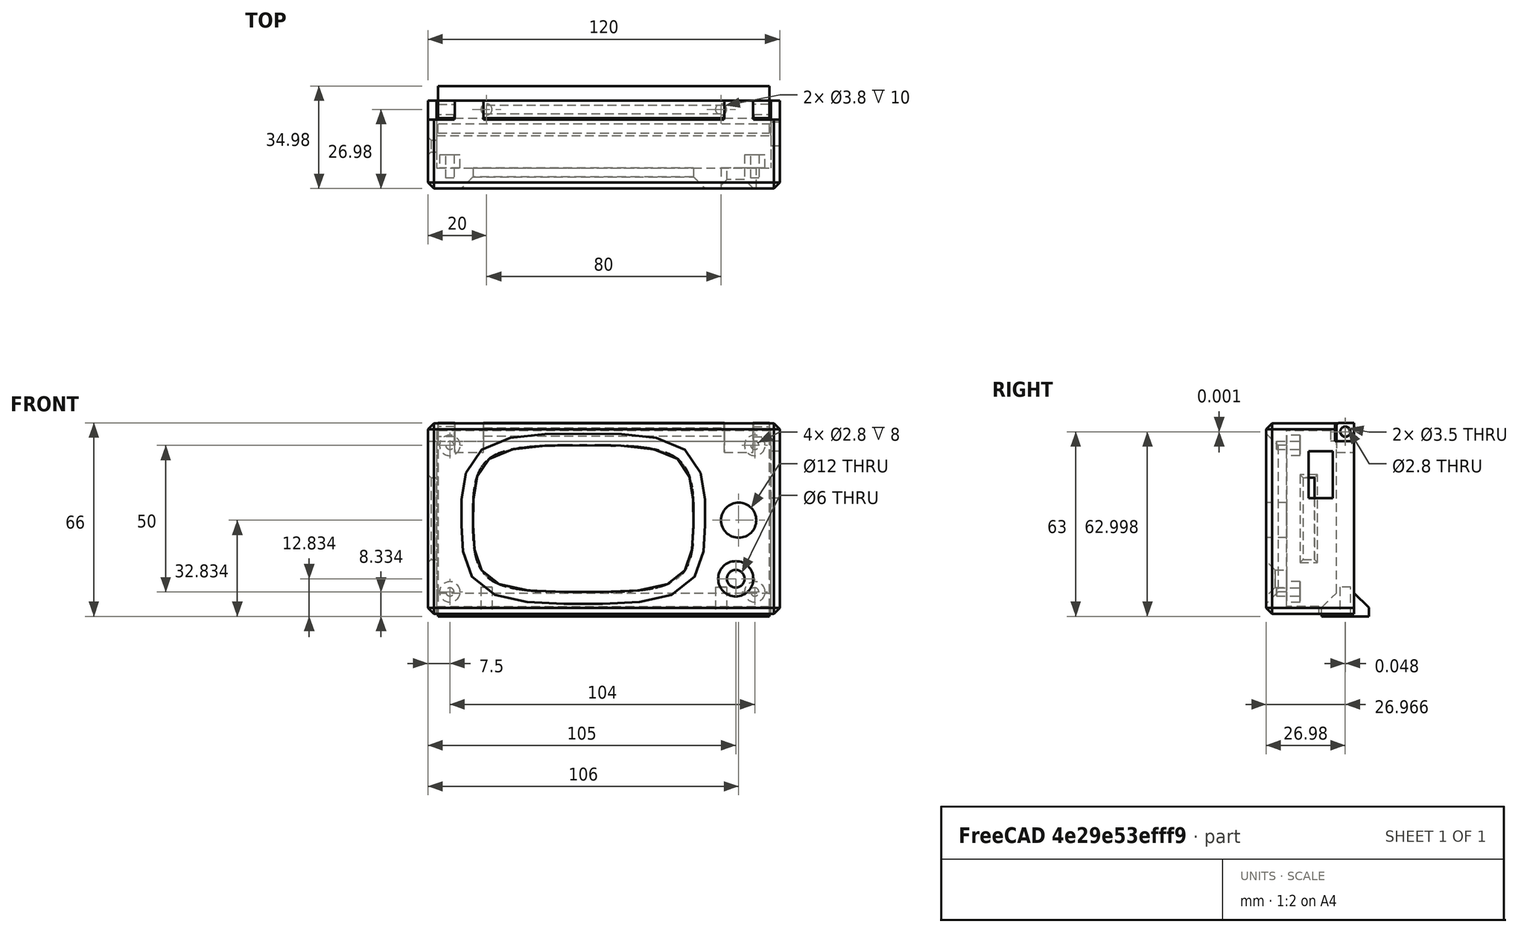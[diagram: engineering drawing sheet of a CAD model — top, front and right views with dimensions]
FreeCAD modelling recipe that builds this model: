
FCSTD DOCUMENT  (FreeCAD 0.19R)
Label: BottomScreen
License: All rights reserved
LicenseURL: http://en.wikipedia.org/wiki/All_rights_reserved
objects: Sketcher::SketchObject×18, PartDesign::Pocket×13, PartDesign::Pad×5, PartDesign::Chamfer×4, PartDesign::Body×2, Mesh::Feature×2, PartDesign::Fillet×1
note: 66 computed .brp shape members not serialized (recipe doc carries the construction recipe); baked Part::Feature solids carry a one-line shape summary decoded from their .brp

FEATURE [Sketcher::SketchObject] Sketch028  label="knob"
  FullyConstrained = false
  MapMode = 5
  Placement = pos=(0,0,0) rot=(1,0,0;3.14159rad)
  sketch-geometry (1):
    g0: Circle CenterX=52 CenterY=20.5 CenterZ=0 NormalX=0 NormalY=0 NormalZ=1 AngleXU=0 Radius=3
  constraints (1):
    c: Diameter(g0) = 6
FEATURE [Sketcher::SketchObject] Sketch029
  FullyConstrained = true
  MapMode = 5
  Support = -> [XY_Plane002]
  sketch-geometry (30):
    g0: LineSegment StartX=-53 StartY=32.5 StartZ=0 EndX=67 EndY=32.5 EndZ=0
    g1: LineSegment StartX=67 StartY=32.5 StartZ=0 EndX=67 EndY=-32.5 EndZ=0
    g2: LineSegment StartX=67 StartY=-32.5 StartZ=0 EndX=-53 EndY=-32.5 EndZ=0
    g3: LineSegment StartX=-53 StartY=-32.5 StartZ=0 EndX=-53 EndY=32.5 EndZ=0
    g4: LineSegment StartX=-37 StartY=24.5 StartZ=0 EndX=37 EndY=24.5 EndZ=0
    g5: LineSegment StartX=37 StartY=24.5 StartZ=0 EndX=37 EndY=-24.5 EndZ=0
    g6: LineSegment StartX=37 StartY=-24.5 StartZ=0 EndX=-37 EndY=-24.5 EndZ=0
    g7: LineSegment StartX=-37 StartY=-24.5 StartZ=0 EndX=-37 EndY=24.5 EndZ=0
    g8: LineSegment StartX=-37.7408 StartY=25.116 StartZ=0 EndX=37.7408 EndY=25.116 EndZ=0
    g9: LineSegment StartX=37.7408 StartY=25.116 StartZ=0 EndX=37.7408 EndY=-25.116 EndZ=0
    g10: LineSegment StartX=37.7408 StartY=-25.116 StartZ=0 EndX=-37.7408 EndY=-25.116 EndZ=0
    g11: LineSegment StartX=-37.7408 StartY=-25.116 StartZ=0 EndX=-37.7408 EndY=25.116 EndZ=0
    g12-g19: Circle x8 (B-spline internal-alignment scaffolding for g20; pole/knot coordinates omitted)
    g20: BSplineCurve PolesCount=8 KnotsCount=9 Degree=3 IsPeriodic=1
    g21-g29: GeomPoint x9 (B-spline internal-alignment scaffolding for g20; pole/knot coordinates omitted)
  constraints (53):
    c: Coincident(g0,g1)
    c: Coincident(g1,g2)
    c: Coincident(g2,g3)
    c: Coincident(g3,g0)
    c: Horizontal(g0)
    c: Horizontal(g2)
    c: Vertical(g1)
    c: Vertical(g3)
    c: Coincident(g4,g5)
    c: Coincident(g5,g6)
    c: Coincident(g6,g7)
    c: Coincident(g7,g4)
    c: Horizontal(g4)
    c: Vertical(g7)
    c: Distance(g5) = 49
    c: Distance(g4,g3) = 16
    c: Distance(g0,g5) = 30
    c: Distance(g6,g2) = 8
    c: Distance(g4,g0) = 8
    c: Distance(g6) = 74
    c: Symmetric(g5,g6,g-2)
    c: Symmetric(g5,g4,g-1)
    c: Coincident(g8,g9)
    c: Coincident(g9,g10)
    c: Coincident(g10,g11)
    c: Coincident(g11,g8)
    c: Horizontal(g8)
    c: Horizontal(g10)
    c: Vertical(g9)
    c: Vertical(g11)
    c: Symmetric(g9,g8,g-1)
    c: Weight(g12) = 1
    c: Equal(g12,g13)
    c: Equal(g12,g14)
    c: Equal(g12,g15)
    c: PointOnObject(g15,g-1)
    c: Equal(g12,g16)
    c: Equal(g12,g17)
    c: PointOnObject(g17,g-2)
    c: Equal(g12,g18)
    c: Equal(g12,g19)
    c: InternalAlignment(g12-g19 -> g20) x8
    c: InternalAlignment(g21-g29 -> g20) x9
    c: Coincident(g8,g12)
    c: Coincident(g14,g8)
    c: Coincident(g16,g10)
    c: Coincident(g18,g9)
    c: Distance(g19,g5) = 0.5
    c: Symmetric(g19,g15,g-2)
    c: Distance(g17,g6) = 0.5
    c: Symmetric(g17,g13,g-1)
    c: DistanceX(g8) = 37.7408
    c: DistanceY(g8) = 25.116
FEATURE [PartDesign::Pad] Pad005
  Direction = (1,1,1)
  Length = 30
  Length2 = 100
  Profile = -> Sketch029
  Type = 0
FEATURE [PartDesign::Pocket] Pocket016
  BaseFeature = -> Pad005
  Length = 5
  Length2 = 100
  Profile = -> Sketch028
  Type = 1
FEATURE [Sketcher::SketchObject] Sketch001  label="knob001"
  FullyConstrained = false
  MapMode = 5
  Placement = pos=(0,0,30) rot=(0,0,1;0rad)
  Support = -> [Pocket016]
  sketch-geometry (1):
    g0: Circle CenterX=53 CenterY=-0.5 CenterZ=0 NormalX=0 NormalY=0 NormalZ=1 AngleXU=0 Radius=6
  constraints (2):
    c: Diameter(g0) = 12
    c: DistanceY(g0) = -0.5
FEATURE [PartDesign::Pocket] Pocket017
  BaseFeature = -> Pocket016
  Length = 5
  Length2 = 100
  Profile = -> Sketch001
  Type = 1
FEATURE [Sketcher::SketchObject] Sketch030  label="BodyPocket"
  ExternalGeometry = -> [Pocket017]
  FullyConstrained = true
  MapMode = 5
  Placement = pos=(0,0,0) rot=(1,0,0;3.14159rad)
  Support = -> [Pocket017]
  sketch-geometry (4):
    g0: LineSegment StartX=-50 StartY=30 StartZ=0 EndX=64 EndY=30 EndZ=0
    g1: LineSegment StartX=64 StartY=30 StartZ=0 EndX=64 EndY=-30 EndZ=0
    g2: LineSegment StartX=64 StartY=-30 StartZ=0 EndX=-50 EndY=-30 EndZ=0
    g3: LineSegment StartX=-50 StartY=-30 StartZ=0 EndX=-50 EndY=30 EndZ=0
  constraints (12):
    c: Coincident(g0,g1)
    c: Coincident(g1,g2)
    c: Coincident(g2,g3)
    c: Coincident(g3,g0)
    c: Horizontal(g0)
    c: Horizontal(g2)
    c: Vertical(g1)
    c: DistanceX(g0) = -50
    c: DistanceY(g0) = 30
    c: DistanceX(g1) = 64
    c: DistanceY(g2) = -30
    c: Vertical(g3)
FEATURE [PartDesign::Pocket] Pocket018
  BaseFeature = -> Pocket017
  Length = 23
  Length2 = 100
  Profile = -> Sketch030
  Type = 0
FEATURE [PartDesign::Chamfer] Chamfer001
  Angle = 45
  Base = -> Pocket018 [Edge19]
  BaseFeature = -> Pocket018
  ChamferType = 0
  FlipDirection = false
  Size = 4
  Size2 = 1
  SupportTransform = false
FEATURE [Sketcher::SketchObject] Sketch031  label="standofs"
  FullyConstrained = true
  MapMode = 5
  Placement = pos=(0,0,23) rot=(1,0,0;3.14159rad)
  Support = -> [Chamfer001]
  sketch-geometry (4):
    g0: Circle CenterX=-45.5 CenterY=25 CenterZ=0 NormalX=0 NormalY=0 NormalZ=1 AngleXU=0 Radius=3.5
    g1: Circle CenterX=-45.5 CenterY=-25 CenterZ=0 NormalX=0 NormalY=0 NormalZ=1 AngleXU=0 Radius=3.5
    g2: Circle CenterX=58.5 CenterY=-25 CenterZ=0 NormalX=0 NormalY=0 NormalZ=1 AngleXU=0 Radius=3.5
    g3: Circle CenterX=58.5 CenterY=25 CenterZ=0 NormalX=0 NormalY=0 NormalZ=1 AngleXU=0 Radius=3.5
  constraints (10):
    c: Diameter(g0) = 7
    c: Equal(g0,g1)
    c: Equal(g0,g3)
    c: Equal(g0,g2)
    c: Symmetric(g1,g0,g-1)
    c: Symmetric(g2,g3,g-1)
    c: Distance(g3,g2) = 50
    c: Distance(g1,g0) = 50
    c: Distance(g3,g0) = 104
    c: DistanceX(g0) = -45.5
FEATURE [PartDesign::Pad] Pad006
  BaseFeature = -> Chamfer001
  Direction = (1,1,1)
  Length = 4.5
  Length2 = 100
  Profile = -> Sketch031
  Type = 0
FEATURE [Sketcher::SketchObject] Sketch032  label="holes"
  FullyConstrained = true
  MapMode = 5
  Placement = pos=(0,0,18.5) rot=(1,0,0;3.14159rad)
  Support = -> [Pad006]
  sketch-geometry (4):
    g0: Circle CenterX=-45.5 CenterY=25 CenterZ=0 NormalX=0 NormalY=0 NormalZ=1 AngleXU=0 Radius=1.4
    g1: Circle CenterX=58.5 CenterY=25 CenterZ=0 NormalX=0 NormalY=0 NormalZ=1 AngleXU=0 Radius=1.4
    g2: Circle CenterX=58.5 CenterY=-25 CenterZ=0 NormalX=0 NormalY=0 NormalZ=1 AngleXU=0 Radius=1.4
    g3: Circle CenterX=-45.5 CenterY=-25 CenterZ=0 NormalX=0 NormalY=0 NormalZ=1 AngleXU=0 Radius=1.4
  constraints (10):
    c: Distance(g3,g2) = 104
    c: Distance(g3,g0) = 50
    c: Symmetric(g3,g0,g-1)
    c: Symmetric(g2,g1,g-1)
    c: Diameter(g1) = 2.8
    c: Equal(g1,g2)
    c: Equal(g1,g3)
    c: Equal(g1,g0)
    c: DistanceX(g0) = -45.5
    c: Distance(g1,g2) = 50
FEATURE [PartDesign::Pocket] Pocket019
  BaseFeature = -> Pad006
  Length = 8
  Length2 = 100
  Profile = -> Sketch032
  Type = 0
FEATURE [Sketcher::SketchObject] Sketch033
  ExternalGeometry = -> [Pocket019]
  FullyConstrained = true
  MapMode = 5
  Placement = pos=(67,0,0) rot=(0.57735,0.57735,0.57735;2.0944rad)
  Support = -> [Pocket019]
  sketch-geometry (4):
    g0: LineSegment StartX=7 StartY=15.5 StartZ=0 EndX=23 EndY=15.5 EndZ=0
    g1: LineSegment StartX=23 StartY=15.5 StartZ=0 EndX=23 EndY=0 EndZ=0
    g2: LineSegment StartX=23 StartY=0 StartZ=0 EndX=7 EndY=0 EndZ=0
    g3: LineSegment StartX=7 StartY=0 StartZ=0 EndX=7 EndY=15.5 EndZ=0
  constraints (12):
    c: Coincident(g0,g1)
    c: Coincident(g1,g2)
    c: Coincident(g2,g3)
    c: Coincident(g3,g0)
    c: Horizontal(g0)
    c: Horizontal(g2)
    c: Vertical(g1)
    c: Vertical(g3)
    c: Distance(g-3,g0) = 3
    c: Distance(g0) = 16
    c: Distance(g0,g-4) = 7
    c: PointOnObject(g1,g-1)
FEATURE [PartDesign::Pocket] Pocket020
  BaseFeature = -> Pocket019
  Length = 9
  Length2 = 100
  Profile = -> Sketch033
  Type = 0
FEATURE [Sketcher::SketchObject] Sketch034  label="SD"
  ExternalGeometry = -> [Pocket020]
  FullyConstrained = true
  MapMode = 5
  Placement = pos=(-53,0,0) rot=(0.57735,-0.57735,-0.57735;2.0944rad)
  Support = -> [Pocket020]
  sketch-geometry (4):
    g0: LineSegment StartX=-14 StartY=17.5 StartZ=0 EndX=14 EndY=17.5 EndZ=0
    g1: LineSegment StartX=14 StartY=17.5 StartZ=0 EndX=14 EndY=13.5 EndZ=0
    g2: LineSegment StartX=14 StartY=13.5 StartZ=0 EndX=-14 EndY=13.5 EndZ=0
    g3: LineSegment StartX=-14 StartY=13.5 StartZ=0 EndX=-14 EndY=17.5 EndZ=0
  constraints (11):
    c: Coincident(g0,g1)
    c: Coincident(g1,g2)
    c: Coincident(g2,g3)
    c: Coincident(g3,g0)
    c: Horizontal(g0)
    c: Vertical(g1)
    c: Vertical(g3)
    c: Distance(g0,g-3) = 1
    c: Distance(g1) = 4
    c: Symmetric(g1,g2,g-2)
    c: Distance(g2) = 28
FEATURE [PartDesign::Pocket] Pocket021
  BaseFeature = -> Pocket020
  Length = 5
  Length2 = 100
  Profile = -> Sketch034
  Type = 0
FEATURE [Sketcher::SketchObject] Sketch041
  FullyConstrained = true
  MapMode = 5
  Placement = pos=(0,0,0) rot=(0.57735,0.57735,0.57735;2.0944rad)
  Support = -> [YZ_Plane]
  sketch-geometry (9):
    g0: LineSegment StartX=-11 StartY=0 StartZ=0 EndX=-11 EndY=3 EndZ=0
    g1: LineSegment StartX=-11 StartY=3 StartZ=0 EndX=-6 EndY=8 EndZ=0
    g2: LineSegment StartX=-6 StartY=8 StartZ=0 EndX=-6 EndY=66 EndZ=0
    g3: LineSegment StartX=-6 StartY=66 StartZ=0 EndX=0 EndY=66 EndZ=0
    g4: LineSegment StartX=-11 StartY=0 StartZ=0 EndX=0 EndY=0 EndZ=0
    g5: LineSegment StartX=0 StartY=66 StartZ=0 EndX=0 EndY=8 EndZ=0
    g6: LineSegment StartX=0 StartY=8 StartZ=0 EndX=5 EndY=3 EndZ=0
    g7: LineSegment StartX=5 StartY=3 StartZ=0 EndX=5 EndY=0 EndZ=0
    g8: LineSegment StartX=0 StartY=0 StartZ=0 EndX=5 EndY=0 EndZ=0
  constraints (26):
    c: PointOnObject(g3,g-2)
    c: DistanceY(g3) = 66
    c: PointOnObject(g0,g-1)
    c: Vertical(g0)
    c: Coincident(g0,g1)
    c: Coincident(g1,g2)
    c: Vertical(g2)
    c: Coincident(g2,g3)
    c: Coincident(g4,g0)
    c: Coincident(g4,g-1)
    c: Horizontal(g3)
    c: DistanceX(g2) = -6
    c: Distance(g4) = 11
    c: Distance(g0) = 3
    c: Angle(g1) = 0.785398
    c: Coincident(g5,g3)
    c: PointOnObject(g5,g-2)
    c: Coincident(g6,g5)
    c: Coincident(g7,g6)
    c: PointOnObject(g7,g-1)
    c: Coincident(g8,g4)
    c: Coincident(g8,g7)
    c: Vertical(g7)
    c: Distance(g7) = 3
    c: Distance(g8) = 5
    c: Angle(g6) = -0.785398
FEATURE [PartDesign::Pad] Pad
  Direction = (1,1,1)
  Length = 113
  Length2 = 100
  Midplane = true
  Placement = pos=(0,0,0) rot=(0.57735,0.57735,0.57735;2.0944rad)
  Profile = -> Sketch041
  Type = 0
FEATURE [Sketcher::SketchObject] Sketch047
  ExternalGeometry = -> [Pocket021]
  FullyConstrained = false
  MapMode = 5
  Placement = pos=(0,-32.5,0) rot=(1,0,0;1.5708rad)
  Support = -> [Pocket021]
  sketch-geometry (4):
    g0: LineSegment StartX=-50 StartY=12 StartZ=0 EndX=64 EndY=12 EndZ=0
    g1: LineSegment StartX=64 StartY=12 StartZ=0 EndX=64 EndY=-7.27201 EndZ=0
    g2: LineSegment StartX=64 StartY=-7.27201 StartZ=0 EndX=-50 EndY=-7.27201 EndZ=0
    g3: LineSegment StartX=-50 StartY=-7.27201 StartZ=0 EndX=-50 EndY=12 EndZ=0
  constraints (11):
    c: Coincident(g0,g1)
    c: Coincident(g1,g2)
    c: Coincident(g2,g3)
    c: Coincident(g3,g0)
    c: Horizontal(g2)
    c: Vertical(g1)
    c: Vertical(g3)
    c: DistanceY(g0) = 12
    c: DistanceX(g0) = -50
    c: DistanceX(g0) = 64
    c: Horizontal(g0)
FEATURE [PartDesign::Pocket] Pocket
  BaseFeature = -> Pocket021
  Length = 5
  Length2 = 100
  Profile = -> Sketch047
  Type = 0
FEATURE [Sketcher::SketchObject] Sketch
  ExternalGeometry = -> [Pocket]
  FullyConstrained = false
  MapMode = 5
  Placement = pos=(0,32.5,0) rot=(0,0.707107,0.707107;3.14159rad)
  Support = -> [Pocket]
  sketch-geometry (20):
    g0: LineSegment StartX=-69.7312 StartY=6.5 StartZ=0 EndX=-58 EndY=6.5 EndZ=0
    g1: LineSegment StartX=-58 StartY=6.5 StartZ=0 EndX=-58 EndY=-6.37632 EndZ=0
    g2: LineSegment StartX=-58 StartY=-6.37632 StartZ=0 EndX=-69.7312 EndY=-6.37632 EndZ=0
    g3: LineSegment StartX=-69.7312 StartY=-6.37632 StartZ=0 EndX=-69.7312 EndY=6.5 EndZ=0
    g4: LineSegment StartX=-48 StartY=-9.0631 StartZ=0 EndX=-48 EndY=6.5 EndZ=0
    g5: LineSegment StartX=-32 StartY=6.5 StartZ=0 EndX=-26 EndY=6.5 EndZ=0
    g6: LineSegment StartX=-26 StartY=6.5 StartZ=0 EndX=-26 EndY=-4.42544 EndZ=0
    g7: LineSegment StartX=-26 StartY=-4.42544 StartZ=0 EndX=-32 EndY=-4.42544 EndZ=0
    g8: LineSegment StartX=-32 StartY=-4.42544 StartZ=0 EndX=-32 EndY=6.5 EndZ=0
    g9: LineSegment StartX=-16 StartY=6.5 StartZ=0 EndX=-10 EndY=6.5 EndZ=0
    g10: LineSegment StartX=-10 StartY=6.5 StartZ=0 EndX=-10 EndY=-4.36785 EndZ=0
    g11: LineSegment StartX=-10 StartY=-4.36785 StartZ=0 EndX=-16 EndY=-4.36785 EndZ=0
    g12: LineSegment StartX=-16 StartY=-4.36785 StartZ=0 EndX=-16 EndY=6.5 EndZ=0
    g13: LineSegment StartX=56.4953 StartY=6.5 StartZ=0 EndX=44 EndY=6.5 EndZ=0
    g14: LineSegment StartX=44 StartY=6.5 StartZ=0 EndX=44 EndY=-6.05703 EndZ=0
    g15: LineSegment StartX=44 StartY=-6.05703 StartZ=0 EndX=56.4953 EndY=-6.05703 EndZ=0
    g16: LineSegment StartX=56.4953 StartY=-6.05703 StartZ=0 EndX=56.4953 EndY=6.5 EndZ=0
    g17: LineSegment StartX=34 StartY=6.5 StartZ=0 EndX=-48 EndY=6.5 EndZ=0
    g18: LineSegment StartX=-48 StartY=-9.0631 StartZ=0 EndX=34 EndY=-9.0631 EndZ=0
    g19: LineSegment StartX=34 StartY=-9.0631 StartZ=0 EndX=34 EndY=6.5 EndZ=0
  constraints (52):
    c: Coincident(g0,g1)
    c: Coincident(g1,g2)
    c: Coincident(g2,g3)
    c: Coincident(g3,g0)
    c: Horizontal(g0)
    c: Horizontal(g2)
    c: Vertical(g1)
    c: Vertical(g3)
    c: Distance(g0,g-3) = 9
    c: DistanceY(g0) = 6.5
    c: Vertical(g4)
    c: DistanceX(g0,g4) = 10
    c: Coincident(g5,g6)
    c: Coincident(g6,g7)
    c: Coincident(g7,g8)
    c: Coincident(g8,g5)
    c: Horizontal(g5)
    c: Horizontal(g7)
    c: Vertical(g6)
    c: Vertical(g8)
    c: Coincident(g9,g10)
    c: Coincident(g10,g11)
    c: Coincident(g11,g12)
    c: Coincident(g12,g9)
    c: Horizontal(g9)
    c: Horizontal(g11)
    c: Vertical(g10)
    c: Vertical(g12)
    c: Distance(g5) = 6
    c: DistanceX(g5,g9) = 10
    c: Distance(g9) = 6
    c: DistanceY(g9) = 6.5
    c: DistanceY(g5) = 6.5
    c: Coincident(g13,g14)
    c: Coincident(g14,g15)
    c: Coincident(g15,g16)
    c: Coincident(g16,g13)
    c: Horizontal(g13)
    c: Horizontal(g15)
    c: Vertical(g14)
    c: Vertical(g16)
    c: Coincident(g18,g19)
    c: Coincident(g19,g17)
    c: Horizontal(g17)
    c: Horizontal(g18)
    c: Vertical(g19)
    c: DistanceY(g17) = 6.5
    c: DistanceY(g13) = 6.5
    c: Distance(g13,g-4) = 9
    c: DistanceX(g17,g13) = 10
    c: Coincident(g18,g4)
    c: Coincident(g17,g4)
FEATURE [Sketcher::SketchObject] Sketch048
  ExternalGeometry = -> [Pocket]
  FullyConstrained = true
  MapMode = 5
  Placement = pos=(0,0,0) rot=(1,0,0;3.14159rad)
  Support = -> [Pocket]
  sketch-geometry (4):
    g0: LineSegment StartX=-53 StartY=-26.5 StartZ=0 EndX=67 EndY=-26.5 EndZ=0
    g1: LineSegment StartX=67 StartY=-26.5 StartZ=0 EndX=67 EndY=-32 EndZ=0
    g2: LineSegment StartX=67 StartY=-32 StartZ=0 EndX=-53 EndY=-32 EndZ=0
    g3: LineSegment StartX=-53 StartY=-32 StartZ=0 EndX=-53 EndY=-26.5 EndZ=0
  constraints (12):
    c: Coincident(g0,g1)
    c: Coincident(g1,g2)
    c: Coincident(g2,g3)
    c: Coincident(g3,g0)
    c: Horizontal(g0)
    c: Horizontal(g2)
    c: Vertical(g1)
    c: Vertical(g3)
    c: DistanceY(g1) = -32
    c: DistanceX(g0) = 67
    c: DistanceX(g0) = -53
    c: Distance(g0,g-3) = 6
FEATURE [PartDesign::Pad] Pad007
  BaseFeature = -> Pocket
  Direction = (1,1,1)
  Length = 8
  Length2 = 100
  Profile = -> Sketch048
  Reversed = true
  Type = 0
FEATURE [PartDesign::Pocket] Pocket032
  BaseFeature = -> Pad007
  Length = 6
  Length2 = 100
  Profile = -> Sketch
  Type = 0
FEATURE [Sketcher::SketchObject] Sketch049
  FullyConstrained = false
  MapMode = 5
  Placement = pos=(-2.56e-14,3.66e-14,66) rot=(0,0,-1;1.5708rad)
  Support = -> [Pad]
  sketch-geometry (16):
    g0: LineSegment StartX=-3.15788 StartY=61.4961 StartZ=0 EndX=6.80578 EndY=61.4961 EndZ=0
    g1: LineSegment StartX=6.80578 StartY=61.4961 StartZ=0 EndX=6.80578 EndY=56.6425 EndZ=0
    g2: LineSegment StartX=6.80578 StartY=56.6425 StartZ=0 EndX=-3.15788 EndY=56.6425 EndZ=0
    g3: LineSegment StartX=-3.15788 StartY=56.6425 StartZ=0 EndX=-3.15788 EndY=61.4961 EndZ=0
    g4: LineSegment StartX=-4.59158 StartY=50.904 StartZ=0 EndX=9.82769 EndY=50.904 EndZ=0
    g5: LineSegment StartX=9.82769 StartY=50.904 StartZ=0 EndX=9.82769 EndY=41.104 EndZ=0
    g6: LineSegment StartX=9.82769 StartY=41.104 StartZ=0 EndX=-4.59158 EndY=41.104 EndZ=0
    g7: LineSegment StartX=-4.59158 StartY=41.104 StartZ=0 EndX=-4.59158 EndY=50.904 EndZ=0
    g8: LineSegment StartX=-6.16671 StartY=-41.0394 StartZ=0 EndX=7.99909 EndY=-41.0394 EndZ=0
    g9: LineSegment StartX=7.99909 StartY=-41.0394 StartZ=0 EndX=7.99909 EndY=-50.8394 EndZ=0
    g10: LineSegment StartX=7.99909 StartY=-50.8394 StartZ=0 EndX=-6.16671 EndY=-50.8394 EndZ=0
    g11: LineSegment StartX=-6.16671 StartY=-50.8394 StartZ=0 EndX=-6.16671 EndY=-41.0394 EndZ=0
    g12: LineSegment StartX=-2.49543 StartY=-56.9158 StartZ=0 EndX=6.75431 EndY=-56.9158 EndZ=0
    g13: LineSegment StartX=6.75431 StartY=-56.9158 StartZ=0 EndX=6.75431 EndY=-60.1158 EndZ=0
    g14: LineSegment StartX=6.75431 StartY=-60.1158 StartZ=0 EndX=-2.49543 EndY=-60.1158 EndZ=0
    g15: LineSegment StartX=-2.49543 StartY=-60.1158 StartZ=0 EndX=-2.49543 EndY=-56.9158 EndZ=0
  constraints (35):
    c: Coincident(g0,g1)
    c: Coincident(g1,g2)
    c: Coincident(g2,g3)
    c: Coincident(g3,g0)
    c: Horizontal(g0)
    c: Horizontal(g2)
    c: Vertical(g1)
    c: Vertical(g3)
    c: Coincident(g4,g5)
    c: Coincident(g5,g6)
    c: Coincident(g6,g7)
    c: Coincident(g7,g4)
    c: Horizontal(g4)
    c: Horizontal(g6)
    c: Vertical(g5)
    c: Vertical(g7)
    c: Coincident(g8,g9)
    c: Coincident(g9,g10)
    c: Coincident(g10,g11)
    c: Coincident(g11,g8)
    c: Horizontal(g8)
    c: Horizontal(g10)
    c: Vertical(g9)
    c: Vertical(g11)
    c: Coincident(g12,g13)
    c: Coincident(g13,g14)
    c: Coincident(g14,g15)
    c: Coincident(g15,g12)
    c: Horizontal(g12)
    c: Horizontal(g14)
    c: Vertical(g13)
    c: Vertical(g15)
    c: Distance(g13) = 3.2
    c: Distance(g9) = 9.8
    c: Distance(g5) = 9.8
FEATURE [PartDesign::Pocket] Pocket033
  BaseFeature = -> Pad
  Length = 10
  Length2 = 100
  Placement = pos=(0,0,0) rot=(0.57735,0.57735,0.57735;2.0944rad)
  Profile = -> Sketch049
  Type = 0
FEATURE [Sketcher::SketchObject] Sketch050
  ExternalGeometry = -> [Pocket033]
  FullyConstrained = true
  MapMode = 5
  Placement = pos=(56.5,-3.76e-14,2.51e-14) rot=(0.57735,0.57735,0.57735;2.0944rad)
  Support = -> [Pocket033]
  sketch-geometry (1):
    g0: Circle CenterX=-3 CenterY=63 CenterZ=0 NormalX=0 NormalY=0 NormalZ=1 AngleXU=0 Radius=1.4
  constraints (3):
    c: DistanceX(g0) = -3
    c: DistanceY(g0) = 63
    c: Diameter(g0) = 2.8
FEATURE [PartDesign::Pocket] Pocket034
  BaseFeature = -> Pocket033
  Length = 5
  Length2 = 100
  Placement = pos=(0,0,0) rot=(0.57735,0.57735,0.57735;2.0944rad)
  Profile = -> Sketch050
  Type = 1
FEATURE [Sketcher::SketchObject] Sketch051
  FullyConstrained = false
  MapMode = 5
  Placement = pos=(56.5,-5.02e-14,3.14e-14) rot=(0.57735,0.57735,0.57735;2.0944rad)
  Support = -> [Pocket034]
  sketch-geometry (1):
    g0: Circle CenterX=-2.96574 CenterY=62.9984 CenterZ=0 NormalX=0 NormalY=0 NormalZ=1 AngleXU=0 Radius=1.75
  constraints (1):
    c: Diameter(g0) = 3.5
FEATURE [PartDesign::Pocket] Pocket035
  BaseFeature = -> Pocket034
  Length = 7
  Length2 = 100
  Placement = pos=(0,0,0) rot=(0.57735,0.57735,0.57735;2.0944rad)
  Profile = -> Sketch051
  Type = 0
FEATURE [Sketcher::SketchObject] Sketch052
  FullyConstrained = false
  MapMode = 5
  Placement = pos=(-56.5,6.27e-14,-3.76e-14) rot=(-0.57735,-0.57735,0.57735;2.0944rad)
  Support = -> [Pocket035]
  sketch-geometry (1):
    g0: Circle CenterX=-3.01386 CenterY=-62.9994 CenterZ=0 NormalX=0 NormalY=0 NormalZ=1 AngleXU=0 Radius=1.75
  constraints (1):
    c: Diameter(g0) = 3.5
FEATURE [PartDesign::Pocket] Pocket036
  BaseFeature = -> Pocket035
  Length = 7
  Length2 = 100
  Placement = pos=(0,0,0) rot=(0.57735,0.57735,0.57735;2.0944rad)
  Profile = -> Sketch052
  Type = 0
FEATURE [Sketcher::SketchObject] Sketch053
  FullyConstrained = true
  MapMode = 5
  Placement = pos=(0,0,6e-14) rot=(0.707107,0.707107,0;3.14159rad)
  Support = -> [Pocket036]
  sketch-geometry (2):
    g0: Circle CenterX=-3 CenterY=40 CenterZ=0 NormalX=0 NormalY=0 NormalZ=1 AngleXU=0 Radius=1.9
    g1: Circle CenterX=-3 CenterY=-40 CenterZ=0 NormalX=0 NormalY=0 NormalZ=1 AngleXU=0 Radius=1.9
  constraints (5):
    c: Symmetric(g1,g0,g-1)
    c: Diameter(g1) = 3.8
    c: Equal(g1,g0)
    c: Distance(g1,g0) = 80
    c: DistanceX(g0) = -3
FEATURE [PartDesign::Pocket] Pocket037
  BaseFeature = -> Pocket036
  Length = 10
  Length2 = 100
  Placement = pos=(0,0,0) rot=(0.57735,0.57735,0.57735;2.0944rad)
  Profile = -> Sketch053
  Type = 0
FEATURE [PartDesign::Fillet] Fillet
  Base = -> Pocket037 [Edge36,Edge40,Edge32]
  BaseFeature = -> Pocket037
  Placement = pos=(0,0,0) rot=(0.57735,0.57735,0.57735;2.0944rad)
  Radius = 1
  SupportTransform = false
FEATURE [PartDesign::Body] Body  label="Hinge"
  Group = -> [Sketch041,Pad,Sketch049,Pocket033,Sketch050,Pocket034,Sketch051,Pocket035,Sketch052,Pocket036,Sketch053,Pocket037,Fillet]
  Origin = -> Origin
  Placement = pos=(-1.5,0,0) rot=(0,0,1;0rad)
  Tip = -> Fillet
FEATURE [PartDesign::Chamfer] Chamfer
  Angle = 45
  Base = -> Pocket032 [Edge19,Edge4,Edge2,Edge42,Edge5,Edge3,Edge27,Edge20]
  BaseFeature = -> Pocket032
  ChamferType = 0
  FlipDirection = false
  Size = 2
  Size2 = 1
  SupportTransform = false
FEATURE [PartDesign::Chamfer] Chamfer002
  Angle = 45
  Base = -> Chamfer [Edge68,Edge66,Edge67,Edge69]
  BaseFeature = -> Chamfer
  ChamferType = 0
  FlipDirection = false
  Size = 1
  Size2 = 1
  SupportTransform = false
FEATURE [PartDesign::Chamfer] Chamfer003
  Angle = 45
  Base = -> Chamfer002 [Edge70]
  BaseFeature = -> Chamfer002
  ChamferType = 0
  FlipDirection = false
  Size = 3
  Size2 = 1
  SupportTransform = false
FEATURE [Sketcher::SketchObject] Sketch054
  FullyConstrained = false
  MapMode = 5
  Placement = pos=(67,0,0) rot=(0.57735,0.57735,0.57735;2.0944rad)
  Support = -> [Chamfer003]
  sketch-geometry (4):
    g0: LineSegment StartX=3.36355 StartY=0 StartZ=0 EndX=24.9272 EndY=0 EndZ=0
    g1: LineSegment StartX=24.9272 StartY=0 StartZ=0 EndX=24.9272 EndY=7.33609 EndZ=0
    g2: LineSegment StartX=24.9272 StartY=7.33609 StartZ=0 EndX=3.36355 EndY=7.33609 EndZ=0
    g3: LineSegment StartX=3.36355 StartY=7.33609 StartZ=0 EndX=3.36355 EndY=0 EndZ=0
  constraints (9):
    c: Coincident(g0,g1)
    c: Coincident(g1,g2)
    c: Coincident(g2,g3)
    c: Coincident(g3,g0)
    c: Horizontal(g0)
    c: Horizontal(g2)
    c: Vertical(g1)
    c: Vertical(g3)
    c: PointOnObject(g0,g-1)
FEATURE [PartDesign::Pad] Pad008
  BaseFeature = -> Chamfer003
  Direction = (1,1,1)
  Length = 3
  Length2 = 100
  Profile = -> Sketch054
  Reversed = true
  Type = 0
FEATURE [PartDesign::Body] Body002  label="ScreenBox"
  Group = -> [Sketch029,Pad005,Sketch001,Sketch028,Pocket016,Pocket017,Sketch030,Pocket018,Chamfer001,Sketch031,Pad006,Sketch032,Pocket019,Sketch033,Pocket020,Sketch034,Pocket021,Sketch047,Pocket,Sketch,Sketch048,Pad007,Pocket032,Chamfer,Chamfer002,Chamfer003,Sketch054,Pad008]
  Origin = -> Origin002
  Placement = pos=(-8.5,0.0221075,33.3342) rot=(-1,0,0;4.71239rad)
  Tip = -> Pad008
FEATURE [Mesh::Feature] Mesh  label="Pad008 (Meshed)"
FEATURE [Mesh::Feature] Mesh001  label="Hinge (Meshed)"
